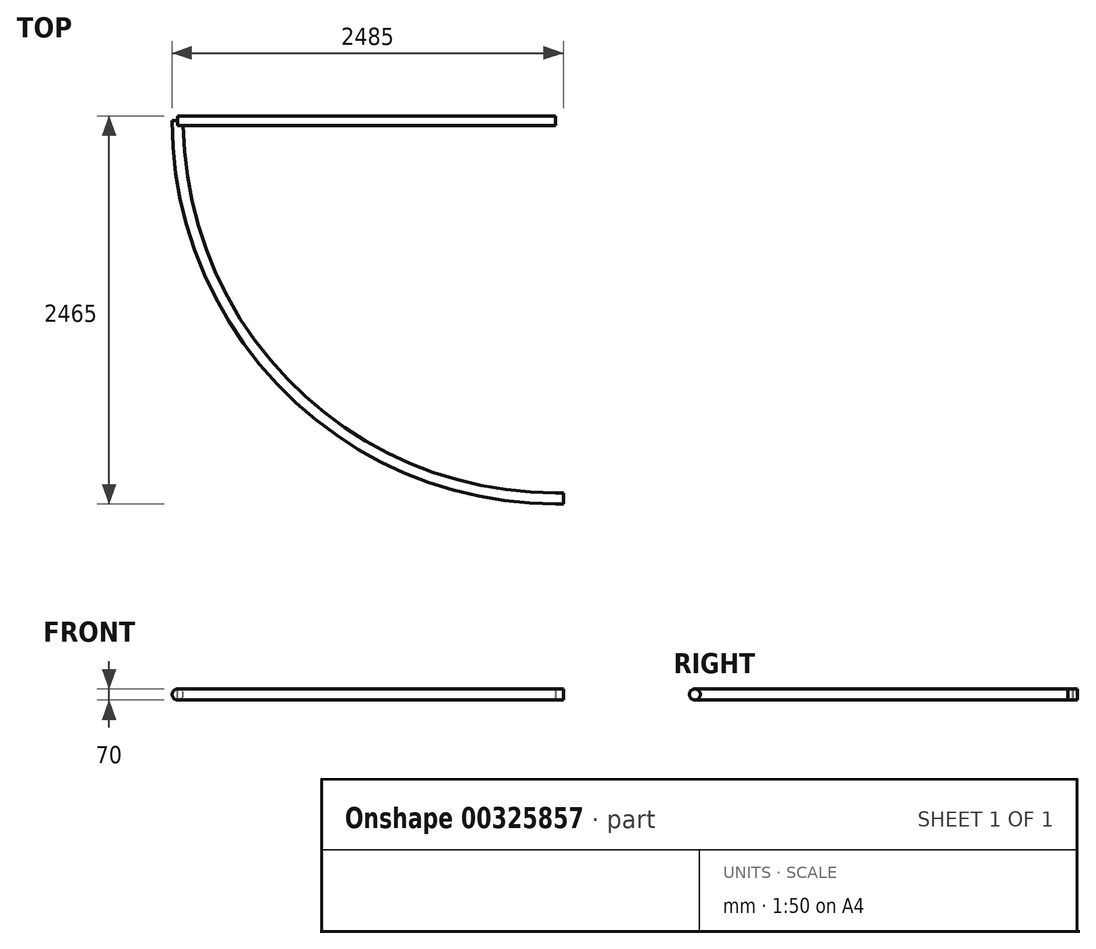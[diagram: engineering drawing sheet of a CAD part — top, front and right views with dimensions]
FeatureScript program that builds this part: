
annotation { "Feature Type Name" : "Feature", "Feature Type Description" : "" }
export const myFeature = defineFeature(function(context is Context, id is Id, definition is map)
    precondition{}
    {
        {
            var Q0;
            Q0=qCreatedBy(makeId("Front.planeOp"),FACE);
            var sketch = newSketch(context, id + "F0", { "sketchPlane" : qUnion([Q0])});
            skCircle(sketch, "E0", {"center": v(-2400, 0) * mm, "radius": 35 * mm});
            skLineSegment(sketch, "E1", {"start": v(0, 0) * mm, "end": v(-2400, 0) * mm, "construction": true});
            skSolve(sketch);
        }
        {
            var Q0;
            Q0=qCreatedBy(makeId("Front.planeOp"),FACE);
            var sketch = newSketch(context, id + "F1", { "sketchPlane" : qUnion([Q0])});
            skLineSegment(sketch, "E2", {"start": v(0, 0) * mm, "end": v(0, 66.65) * mm, "construction": true});
            skSolve(sketch);
        }
        {
            var Q0;
            Q0=makeQuery(id+"F0.imprint","IMPRINT",FACE,{"disambiguationData":[TD([[makeQuery(id+"F0.imprint","IMPRINT",EDGE,{"derivedFrom":sQuery(id+"F0.wireOp",EDGE,"E0")}),1.0]])]});
            var Q1;
            Q1=sQuery(id+"F1.wireOp",EDGE,"E2");
            revolve(context, id + "F2", {"entities" : qUnion([Q0]), "axis" : qUnion([Q1]), "revolveType" : RevolveType.ONE_DIRECTION, "angle" : 90 * degree});
        }
        {
            var Q0;
            Q0=qCreatedBy(makeId("Right.planeOp"),FACE);
            var sketch = newSketch(context, id + "F3", { "sketchPlane" : qUnion([Q0])});
            skLineSegment(sketch, "E3.bottom", {"start": v(30, 35) * mm, "end": v(-30, 35) * mm});
            skLineSegment(sketch, "E3.top", {"start": v(30, -35) * mm, "end": v(-30, -35) * mm});
            skLineSegment(sketch, "E3.left", {"start": v(30, 35) * mm, "end": v(30, -35) * mm});
            skLineSegment(sketch, "E3.right", {"start": v(-30, 35) * mm, "end": v(-30, -35) * mm});
            skPoint(sketch, "E3.middle", {"position": v(0, 0) * mm});
            skSolve(sketch);
        }
        {
            var Q0;
            Q0=makeQuery(id+"F3.imprint","IMPRINT",FACE,{"disambiguationData":[TD([[makeQuery(id+"F3.imprint","IMPRINT",EDGE,{"derivedFrom":sQuery(id+"F3.wireOp",EDGE,"E3.bottom")}),1.0]])]});
            extrude(context, id + "F4", {"entities" : qUnion([Q0]), "operationType" : NewBodyOperationType.ADD, "oppositeDirection" : true, "depth" : 2400 * mm});
        }
        {
            var Q0;
            Q0=makeQuery(id+"F2.opRevolve","CAP_FACE",FACE,{"disambiguationData":[OSD([sQuery(id+"F0.wireOp",EDGE,"E0")])],"isStart":false});
            var sketch = newSketch(context, id + "F5", { "sketchPlane" : qUnion([Q0])});
            skCircle(sketch, "E4", {"center": v(-2400, 0) * mm, "radius": 35 * mm});
            skSolve(sketch);
        }
        {
            var Q0;
            Q0=makeQuery(id+"F5.imprint","IMPRINT",FACE,{"disambiguationData":[TD([[makeQuery(id+"F5.imprint","IMPRINT",EDGE,{"derivedFrom":sQuery(id+"F5.wireOp",EDGE,"E4")}),1.0]])]});
            extrude(context, id + "F6", {"entities" : qUnion([Q0]), "operationType" : NewBodyOperationType.ADD, "depth" : 50 * mm});
        }
    });
